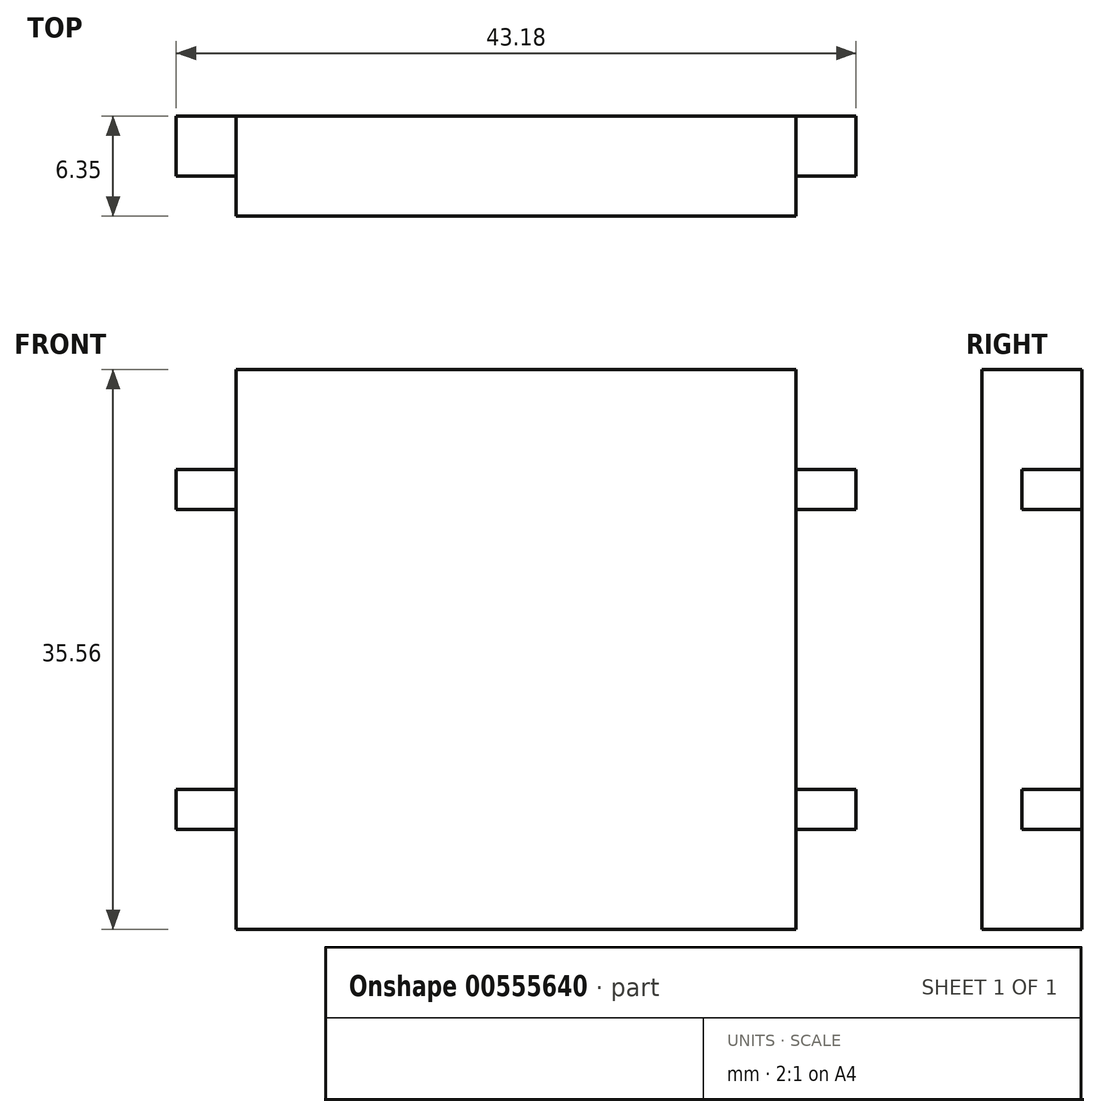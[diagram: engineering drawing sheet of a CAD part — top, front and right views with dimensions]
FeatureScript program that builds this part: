
annotation { "Feature Type Name" : "Feature", "Feature Type Description" : "" }
export const myFeature = defineFeature(function(context is Context, id is Id, definition is map)
    precondition{}
    {
        {
            var Q0;
            Q0=qCreatedBy(makeId("Front.planeOp"),FACE);
            var sketch = newSketch(context, id + "F0", { "sketchPlane" : qUnion([Q0])});
            skLineSegment(sketch, "E0.bottom", {"start": v(17.78, -17.78) * mm, "end": v(-17.78, -17.78) * mm});
            skLineSegment(sketch, "E0.top", {"start": v(17.78, 17.78) * mm, "end": v(-17.78, 17.78) * mm});
            skLineSegment(sketch, "E0.left", {"start": v(17.78, -17.78) * mm, "end": v(17.78, 17.78) * mm});
            skLineSegment(sketch, "E0.right", {"start": v(-17.78, -17.78) * mm, "end": v(-17.78, 17.78) * mm});
            skPoint(sketch, "E0.middle", {"position": v(0, 0) * mm});
            skSolve(sketch);
        }
        {
            var Q0;
            Q0 = qSketchRegion(id + "F0", true);
            extrude(context, id + "F1", {"entities" : qUnion([Q0]), "depth" : 6.35 * mm, "offsetDistance" : 25.4 * mm});
        }
        {
            var Q0;
            Q0=makeQuery(id+"F1.opExtrude","SWEPT_FACE",FACE,{"disambiguationData":[OSD([sQuery(id+"F0.wireOp",EDGE,"E0.left")])]});
            var sketch = newSketch(context, id + "F2", { "sketchPlane" : qUnion([Q0])});
            skLineSegment(sketch, "E1.bottom", {"start": v(0, 11.43) * mm, "end": v(-3.8, 11.43) * mm});
            skLineSegment(sketch, "E1.top", {"start": v(0, 8.9) * mm, "end": v(-3.8, 8.9) * mm});
            skLineSegment(sketch, "E1.left", {"start": v(0, 11.43) * mm, "end": v(0, 8.9) * mm});
            skLineSegment(sketch, "E1.right", {"start": v(-3.81, 11.43) * mm, "end": v(-3.8, 8.9) * mm});
            skLineSegment(sketch, "E2.bottom", {"start": v(0, -8.89) * mm, "end": v(-3.81, -8.89) * mm});
            skLineSegment(sketch, "E2.top", {"start": v(0, -11.43) * mm, "end": v(-3.81, -11.43) * mm});
            skLineSegment(sketch, "E2.left", {"start": v(0, -8.89) * mm, "end": v(0, -11.43) * mm});
            skLineSegment(sketch, "E2.right", {"start": v(-3.81, -8.89) * mm, "end": v(-3.81, -11.43) * mm});
            skSolve(sketch);
        }
        {
            var Q0;
            Q0=makeQuery(id+"F2.imprint","IMPRINT",FACE,{"disambiguationData":[TD([[makeQuery(id+"F2.imprint","IMPRINT",EDGE,{"derivedFrom":sQuery(id+"F2.wireOp",EDGE,"E1.bottom")}),1.0]])]});
            var Q1;
            Q1=makeQuery(id+"F2.imprint","IMPRINT",FACE,{"disambiguationData":[TD([[makeQuery(id+"F2.imprint","IMPRINT",EDGE,{"derivedFrom":sQuery(id+"F2.wireOp",EDGE,"E2.bottom")}),1.0]])]});
            extrude(context, id + "F3", {"entities" : qUnion([Q0, Q1]), "operationType" : NewBodyOperationType.ADD, "depth" : 3.8 * mm, "offsetDistance" : 25.4 * mm});
        }
        {
            var Q0;
            Q0=makeQuery(id+"F1.opExtrude","SWEPT_FACE",FACE,{"disambiguationData":[OSD([sQuery(id+"F0.wireOp",EDGE,"E0.right")])]});
            var sketch = newSketch(context, id + "F4", { "sketchPlane" : qUnion([Q0])});
            skLineSegment(sketch, "E3.bottom", {"start": v(0, 11.43) * mm, "end": v(3.81, 11.43) * mm});
            skLineSegment(sketch, "E3.top", {"start": v(0, 8.9) * mm, "end": v(3.81, 8.9) * mm});
            skLineSegment(sketch, "E3.left", {"start": v(0, 11.43) * mm, "end": v(0, 8.9) * mm});
            skLineSegment(sketch, "E3.right", {"start": v(3.81, 11.43) * mm, "end": v(3.81, 8.9) * mm});
            skLineSegment(sketch, "E4.bottom", {"start": v(0, -11.43) * mm, "end": v(3.81, -11.43) * mm});
            skLineSegment(sketch, "E4.top", {"start": v(0, -8.9) * mm, "end": v(3.8, -8.9) * mm});
            skLineSegment(sketch, "E4.left", {"start": v(0, -11.43) * mm, "end": v(0, -8.9) * mm});
            skLineSegment(sketch, "E4.right", {"start": v(3.81, -11.43) * mm, "end": v(3.8, -8.9) * mm});
            skSolve(sketch);
        }
        {
            var Q0;
            Q0 = qSketchRegion(id + "F4", true);
            extrude(context, id + "F5", {"entities" : qUnion([Q0]), "operationType" : NewBodyOperationType.ADD, "depth" : 3.8 * mm, "offsetDistance" : 25.4 * mm});
        }
    });
